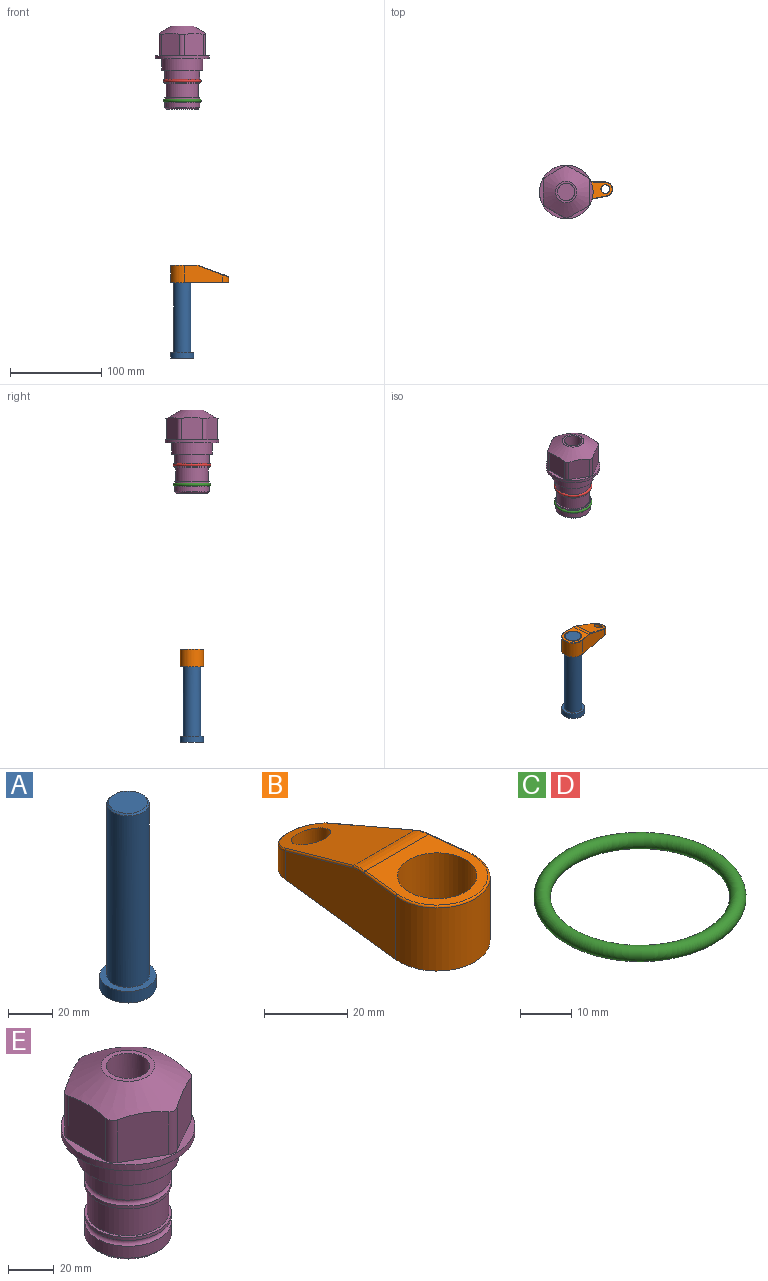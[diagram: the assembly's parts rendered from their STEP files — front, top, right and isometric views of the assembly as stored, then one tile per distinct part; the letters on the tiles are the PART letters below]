
ASSEMBLY  parts=5 mates=3
PART A: 6 faces, bbox 25.4x25.4x101.6 mm
  f0: plane 17.46x17.46mm, normal (0,0,1), area 239.5mm2, adj f5
  f1: plane 25.4x25.4mm, normal (0,0,-1), area 506.7mm2, adj f2
  f2: cylinder r=12.7mm len=25.4mm, axis (0,0,1), area 506.7mm2, adj f1,f3
  f3: plane 25.4x25.4mm, normal (0,0,1), area 221.7mm2, adj f2,f4
  f4: cylinder r=9.53mm len=94.46mm, axis (0,0,1), area 5653mm2, adj f3,f5
  f5: cone r=8.73mm half-angle=45deg, axis (0,0,-1), area 64.4mm2, adj f0,f4
PART B: 44 faces, bbox 27.5x64.5x19.1 mm
  f0: plane 2.3x0.95mm, normal (0,0,-1), area 1mm2, adj f25,f30,f34
  f1: plane 63.5x25.4mm, normal (0,0,-1), area 561.7mm2, adj f2,f3,f4,f5,f6,f7,f19,f20
  f2: cylinder r=12.7mm len=25.4mm, axis (0,0,-1), area 792.2mm2, adj f1,f3,f5,f13
  f3: plane 42.33x18.54mm, normal (0.99,0.11,0), area 647mm2, adj f1,f2,f4,f11,f12,f14
  f4: cylinder r=7.94mm len=15.78mm, axis (0,0,-1), area 158.6mm2, adj f1,f3,f5,f16
  f5: plane 42.33x18.54mm, normal (-0.99,0.11,0), area 647mm2, adj f1,f2,f4,f15,f17,f18
  f6: cylinder r=9.53mm len=19.05mm, axis (0,0,-1), area 1140.1mm2, adj f1,f8
  f7: cylinder r=4.76mm len=10.98mm, axis (0,0,-1), area 276.1mm2, adj f1,f9
  f8: plane 25.83x24.38mm, normal (0,0,1), area 262.2mm2, adj f6,f10,f11,f13,f15
  f9: plane 32.49x20.55mm, normal (0,0.34,0.94), area 489.9mm2, adj f7,f10,f14,f16,f18
  f10: cylinder r=12.7mm len=21.49mm, axis (-1,0,0), area 93.2mm2, adj f8,f9,f12,f17
  f11: cylinder r=0.51mm len=12.34mm, axis (0.11,-0.99,0), area 9.9mm2, adj f3,f8,f12,f13
  f12: bspline ~7.62x1.64mm, area 3.5mm2, adj f3,f10,f11,f14
  f13: torus R=12.19mm, axis (0,0,1), area 33.6mm2, adj f2,f8,f11,f15
  f14: cylinder r=0.51mm len=26.01mm, axis (0.1,-0.93,0.34), area 21.6mm2, adj f3,f9,f12,f16
  f15: cylinder r=0.51mm len=12.34mm, axis (0.11,0.99,0), area 9.9mm2, adj f5,f8,f13,f17
  f16: bspline ~15.78x7.05mm, area 15.7mm2, adj f4,f9,f14,f18
  f17: bspline ~7.62x1.64mm, area 3.5mm2, adj f5,f10,f15,f18
  f18: cylinder r=0.51mm len=26.01mm, axis (0.1,0.93,-0.34), area 21.6mm2, adj f5,f9,f16,f17
  f19: plane 21.6x14.29mm, normal (-0.99,-0.11,0), area 242.6mm2, adj f1,f26,f28,f34,f36,f38
  f20: plane 21.6x14.29mm, normal (0.99,-0.11,0), area 242.6mm2, adj f1,f27,f29,f37,f39,f41
  f21: cylinder r=12.7mm len=14.29mm, axis (0,0,-1), area 173.2mm2, adj f1,f26,f27,f30,f31,f33
  f22: cylinder r=7.94mm len=7.63mm, axis (0,0,-1), area 53.8mm2, adj f1,f28,f29,f42
  f23: plane 2.3x0.95mm, normal (0,0,-1), area 1mm2, adj f25,f33,f37
  f24: plane 17.94x12.32mm, normal (0,-0.34,-0.94), area 191.2mm2, adj f25,f38,f41,f42
  f25: cylinder r=9.53mm len=12.93mm, axis (-1,0,0), area 37.5mm2, adj f0,f23,f24,f31,f36,f39
  f26: cylinder r=1.59mm len=14.29mm, axis (0,0,-1), area 49mm2, adj f1,f19,f21,f32
  f27: cylinder r=1.59mm len=14.29mm, axis (0,0,-1), area 49mm2, adj f1,f20,f21,f35
  f28: cylinder r=1.59mm len=7.28mm, axis (0,0,-1), area 22.1mm2, adj f1,f19,f22,f40
  f29: cylinder r=1.59mm len=7.28mm, axis (0,0,-1), area 22.1mm2, adj f1,f20,f22,f43
  f30: torus R=14.29mm, axis (0,0,1), area 5.8mm2, adj f0,f21,f31,f32
  f31: bspline ~11.06x2.73mm, area 20.8mm2, adj f21,f25,f30,f33
  f32: sphere r=1.59mm, area 5.4mm2, adj f26,f30,f34
  f33: torus R=14.29mm, axis (0,0,1), area 5.8mm2, adj f21,f23,f31,f35
  f34: cylinder r=1.59mm len=1.68mm, axis (-0.11,0.99,0), area 2.4mm2, adj f0,f19,f32,f36
  f35: sphere r=1.59mm, area 5.4mm2, adj f27,f33,f37
  f36: bspline ~5.82x2.33mm, area 7.7mm2, adj f19,f25,f34,f38
  f37: cylinder r=1.59mm len=1.68mm, axis (0.11,0.99,0), area 2.4mm2, adj f20,f23,f35,f39
  f38: cylinder r=1.59mm len=18.33mm, axis (0.1,-0.93,0.34), area 46.7mm2, adj f19,f24,f36,f40
  f39: bspline ~5.82x2.33mm, area 7.7mm2, adj f20,f25,f37,f41
  f40: sphere r=1.59mm, area 3.6mm2, adj f28,f38,f42
  f41: cylinder r=1.59mm len=18.33mm, axis (0.1,0.93,-0.34), area 46.7mm2, adj f20,f24,f39,f43
  f42: bspline ~8.31x1.84mm, area 15.3mm2, adj f22,f24,f40,f43
  f43: sphere r=1.59mm, area 3.6mm2, adj f29,f41,f42
PART C: 1 faces, bbox 44.7x44.7x3.2 mm
  f0: torus R=19.05mm, axis (0,0,1), area 1193.9mm2
PART D: same geometry as C
PART E: 36 faces, bbox 58.7x58.7x91.2 mm
  f0: cylinder r=17.78mm len=35.56mm, axis (0,0,1), area 1670.8mm2, adj f23,f24,f31
  f1: cylinder r=19.05mm len=38.1mm, axis (0,0,1), area 1191.9mm2, adj f26,f27,f30
  f2: plane 58.66x58.66mm, normal (0,0,-1), area 1150.6mm2, adj f3,f28
  f3: cylinder r=29.33mm len=58.66mm, axis (0,0,-1), area 585.1mm2, adj f2,f4
  f4: plane 58.66x58.66mm, normal (0,0,1), area 475.9mm2, adj f3,f5,f6,f7,f8,f9,f10,f11
  f5: plane 24.5x20.32mm, normal (-0.5,0.87,0), area 562.8mm2, adj f4,f15,f16,f17
  f6: plane 24.5x20.32mm, normal (0.5,0.87,0), area 562.8mm2, adj f4,f14,f15,f17
  f7: plane 24.5x23.48mm, normal (1,0,0), area 562.8mm2, adj f4,f13,f14,f17
  f8: plane 24.5x20.32mm, normal (0.5,-0.87,0), area 562.8mm2, adj f4,f12,f13,f17
  f9: plane 24.5x20.32mm, normal (-0.5,-0.87,0), area 562.8mm2, adj f4,f11,f12,f17
  f10: plane 24.5x23.48mm, normal (-1,0,0), area 562.8mm2, adj f4,f11,f16,f17
  f11: cylinder r=5.08mm len=23.01mm, axis (0,0,-1), area 121.2mm2, adj f4,f9,f10,f17
  f12: cylinder r=5.08mm len=23.01mm, axis (0,0,-1), area 121.2mm2, adj f4,f8,f9,f17
  f13: cylinder r=5.08mm len=23.01mm, axis (0,0,-1), area 121.2mm2, adj f4,f7,f8,f17
  f14: cylinder r=5.08mm len=23.01mm, axis (0,0,-1), area 121.2mm2, adj f4,f6,f7,f17
  f15: cylinder r=5.08mm len=23.01mm, axis (0,0,-1), area 121.2mm2, adj f4,f5,f6,f17
  f16: cylinder r=5.08mm len=23.01mm, axis (0,0,-1), area 121.2mm2, adj f4,f5,f10,f17
  f17: cone r=11.73mm half-angle=60deg, axis (0,0,-1), area 2071.8mm2, adj f5,f6,f7,f8,f9,f10,f11,f12
  f18: plane 23.46x23.46mm, normal (0,0,1), area 147.4mm2, adj f17,f35
  f19: plane 34.93x34.93mm, normal (0,0,-1), area 958mm2, adj f29
  f20: cylinder r=19.05mm len=38.1mm, axis (0,0,1), area 760.1mm2, adj f21,f29
  f21: torus R=19.05mm, axis (0,0,1), area 565.3mm2, adj f20,f22
  f22: cylinder r=19.05mm len=38.1mm, axis (0,0,1), area 190mm2, adj f21,f23
  f23: plane 38.1x38.1mm, normal (0,0,1), area 146.9mm2, adj f0,f22
  f24: plane 38.1x38.1mm, normal (0,0,-1), area 146.9mm2, adj f0,f25
  f25: cylinder r=19.05mm len=38.1mm, axis (0,0,1), area 190mm2, adj f24,f26
  f26: torus R=19.05mm, axis (0,0,1), area 565.3mm2, adj f1,f25
  f27: plane 44.45x44.45mm, normal (0,0,-1), area 411.7mm2, adj f1,f28
  f28: cylinder r=22.23mm len=44.45mm, axis (0,0,1), area 1773.5mm2, adj f2,f27
  f29: cone r=19.05mm half-angle=45deg, axis (0,0,1), area 257.5mm2, adj f19,f20
  f30: cylinder r=3.17mm len=6.75mm, axis (-1,0,0), area 128mm2, adj f1,f33
  f31: cylinder r=3.17mm len=6.35mm, axis (-1,0,0), area 102.5mm2, adj f0,f33
  f32: plane 25.4x25.4mm, normal (0,0,1), area 506.7mm2, adj f33
  f33: cylinder r=12.7mm len=66.42mm, axis (0,0,-1), area 5236.2mm2, adj f30,f31,f32,f34
  f34: cone r=9.53mm half-angle=30deg, axis (0,0,-1), area 443.4mm2, adj f33,f35
  f35: cylinder r=9.53mm len=19.05mm, axis (0,0,-1), area 849mm2, adj f18,f34
PLACE A rot(axis=(0,0,1),4.7deg) t=(0,0,-299.6)mm
PLACE B rot(axis=(0,0,-1),85.3deg) t=(0,0,-244.99)mm
PLACE C t=(0,0,-21.59)mm
PLACE D at identity
PLACE E at identity fixed
MATE fastened C.f0 <-> E.f0  axis (0,0,1) through (0,0,-46.1)mm
MATE cylindrical A.f2 <-> E.f0  axis (0,0,1) through (0,0,-273.96)mm
MATE fastened B.f2 <-> A.f2  axis (0,0,1) through (0,0,-225.94)mm
